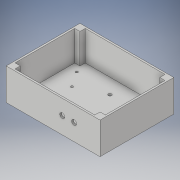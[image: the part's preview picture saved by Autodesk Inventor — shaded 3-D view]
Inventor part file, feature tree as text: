
AUTODESK INVENTOR PART (.ipt)
format: ipt  version: 2018 (Build 220112000, 112)  size: 176,128 bytes
history: native  units: in
note: dims shown in document units (in); Inventor stores cm internally (conversion verified against a paired STEP export)
features: extrude x5, sketch x5
ambient origin geometry x8: Origin, YZ Plane, XZ Plane, XY Plane, X Axis, Y Axis, Z Axis, Center Point
bodies: Solid1 (feature_tree)
feature tree (10):
  extrude  "Extrusion1"  Depth=3.701in
  extrude  "Extrusion2"  Depth=4.527in
  extrude  "Extrusion3"  Depth=0.354in
  sketch  "Sketch7"  dims[d7=0.354in d10=0.354in]
  extrude  "Extrusion7"  Depth=0.354in
  extrude  "Extrusion8"  Depth=1.5in TaperAngle=0.0deg
  sketch  "Sketch1"  dims[d0=4.705in d1=3.701in]
  sketch  "Sketch2"  dims[d2=0.089in d3=0.0in d4=4.527in]
  sketch  "Sketch3"  dims[d5=3.523in d6=0.354in]
  sketch  "Sketch8"  dims[d11=0.354in d14=1.5in d15=0.0in d18=0.164in d19=0.164in d20=0.0in d21=0.0in d48=0.787in d49=0.118in d50=0.118in d51=0.118in d52=0.118in d74=0.25in d75=0.25in d76=0.0in d77=0.0in d78=3.7188in d79=2.3906in d80=0.04in d81=0.04in d82=0.04in d83=0.04in d84=0.04in d85=0.04in d86=0.04in d87=0.04in d88=0.12in d89=0.12in d90=0.12in d91=0.12in d92=0.0in d93=0.0in]
